# Revit family: Toilet_System-Wall_Hung-American_Standard-Afwall-Flushometer-2859_Series
name_source: partatom
category: Plumbing Fixtures
revit_build: Autodesk Revit 2014 (Build: 20130308_1515(x64)
units: mm (PartAtom-declared; Revit-internal decimal feet)

## types (3) — shared parameters
ADA Compliant = Yes
Assembly Code = D2010110
Bowl Shape = Elongated
CW Connection = Yes
CWFU = 10
Cold Water Connection Diameter = 1"
Cold Water Connection Radius = 1/2"
Default Elevation = 15"
Flush Rate = 1.1gpf (4.2Lpf to 6.0 Lpf)
HW Connection = No
Height = 13"
Installation Type = Wall Mounted
Length = 26"
Manufacturer = American Standard
Material = Vitreous China-American Standard-020-White
Price = Prices may vary. Please consult Manufacturer Representative for most up-to-date price list.
Product Documentation Link = https://www.americanstandard-us.com
Product Page URL = https://www.americanstandard-us.com
Revised Date = 02/22/2017
URL = http://www.americanstandard-us.com
Vent Connection = No
WFU = 10
Warranty Information = 1 Year (Limited)
Waste Connection = Yes
Waste Connection Diameter = 2 1/8"
Waste Connection Radius = 1 1/16"
Width = 14"
zero-valued in all types: HWFU

## per-type parameters (varying)
| type | Description |
| 2859.016 | Afwall Millenium Flowise 1.6 GPF Top Spud Bowl, Flushometer Toilet System with everclean Manual flush valve. |
| 2859.111 | Afwall Millenium Flowise 1.1 GPF Top Spud Bowl, Flushometer Toilet System with everclean Manual flush valve. |
| 2859.128 | Afwall Millenium Flowise 1.28 GPF Top Spud Bowl, Flushometer Toilet System with everclean Manual flush valve. |

note: column(s) folded — value = type name in every type: Model

## geometry (parser evidence)
native form markers: Sweep x2
no freeform markers — native parametric forms only
